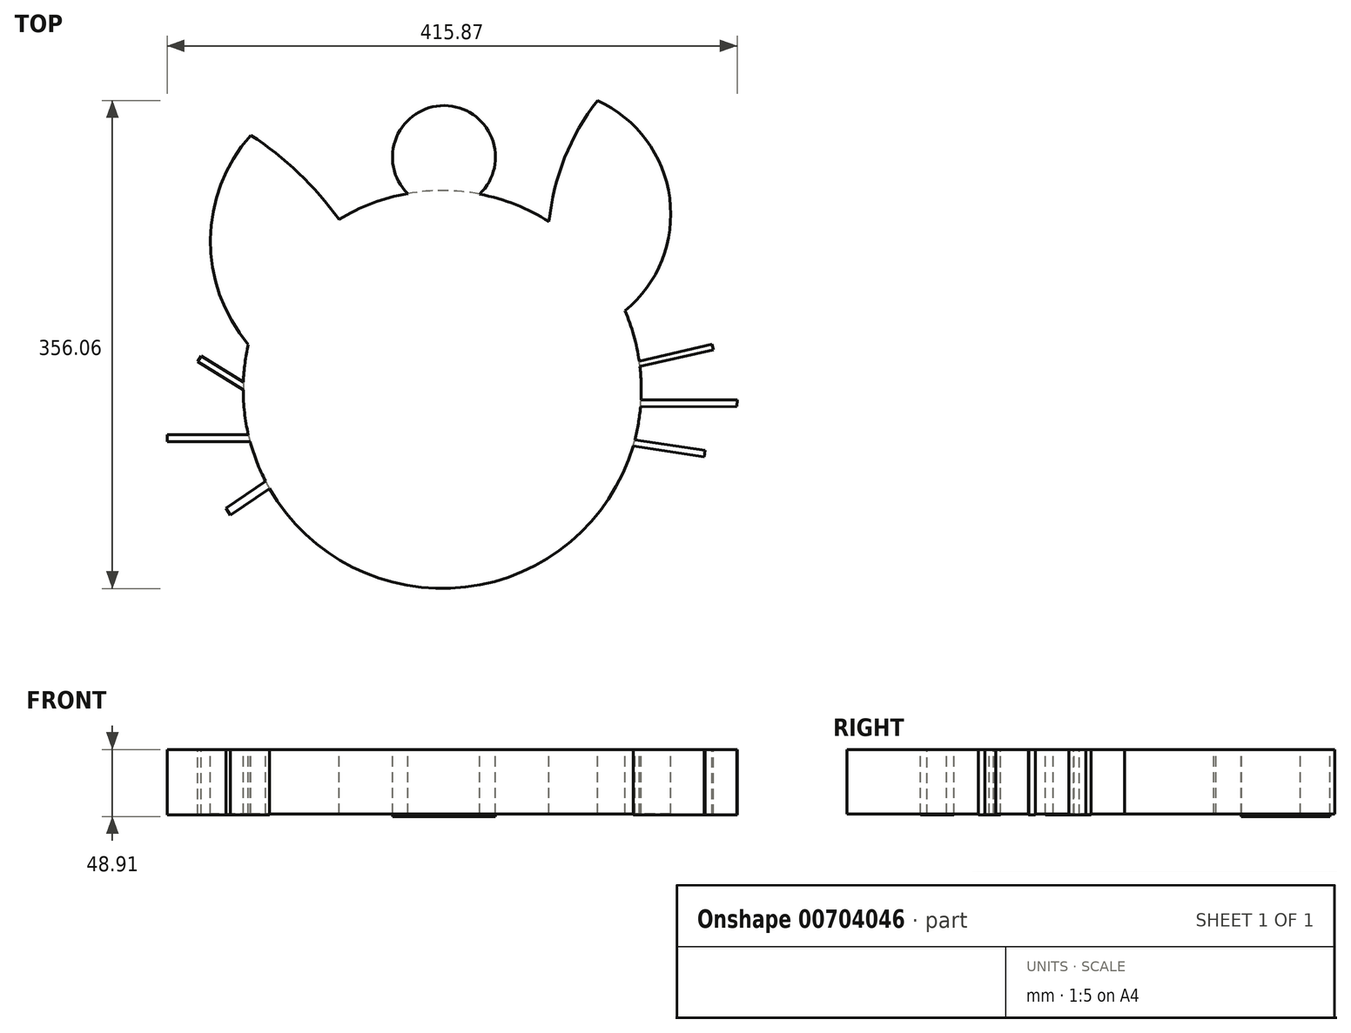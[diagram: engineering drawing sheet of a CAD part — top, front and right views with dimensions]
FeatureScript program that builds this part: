
annotation { "Feature Type Name" : "Feature", "Feature Type Description" : "" }
export const myFeature = defineFeature(function(context is Context, id is Id, definition is map)
    precondition{}
    {
        {
            var Q0;
            Q0=qCreatedBy(makeId("Top.planeOp"),FACE);
            var sketch = newSketch(context, id + "F0", { "sketchPlane" : qUnion([Q0])});
            skCircle(sketch, "E0", {"center": v(70.2, 0) * mm, "radius": 145.22 * mm});
            skArc(sketch, "E1", {"start": v(-5.15, 124.14) * mm, "mid": v(-34.4, 157.96) * mm, "end": v(-69.52, 185.64) * mm});
            skArc(sketch, "E2", {"start": v(-69.52, 185.64) * mm, "mid": v(-98.93, 109.6) * mm, "end": v(-71.24, 32.92) * mm});
            skArc(sketch, "E3", {"start": v(183.54, 210.84) * mm, "mid": v(159.56, 169.2) * mm, "end": v(148.16, 122.52) * mm});
            skArc(sketch, "E4", {"start": v(203.57, 57.46) * mm, "mid": v(236.16, 139.71) * mm, "end": v(183.54, 210.84) * mm});
            skSolve(sketch);
        }
        {
            var Q0;
            Q0 = qSketchRegion(id + "F0", true);
            extrude(context, id + "F1", {"entities" : qUnion([Q0]), "oppositeDirection" : true, "depth" : 46.98 * mm, "offsetDistance" : 25.4 * mm});
        }
        {
            var Q0;
            Q0=makeQuery(id+"F1.opExtrude","CAP_FACE",FACE,{"disambiguationData":[OSD([sQuery(id+"F0.wireOp",EDGE,"E0"),sQuery(id+"F0.wireOp",EDGE,"E1"),sQuery(id+"F0.wireOp",EDGE,"E2"),sQuery(id+"F0.wireOp",EDGE,"E3"),sQuery(id+"F0.wireOp",EDGE,"E4")])],"isStart":true});
            var sketch = newSketch(context, id + "F2", { "sketchPlane" : qUnion([Q0])});
            skArc(sketch, "E5", {"start": v(97.55, 142.62) * mm, "mid": v(71.76, 207.25) * mm, "end": v(45, 143.01) * mm});
            skSolve(sketch);
        }
        {
            var Q0;
            {var subQ0=sQuery(id+"F2.wireOp",EDGE,"E5");Q0=makeQuery(id+"F2.imprint","IMPRINT",FACE,{"disambiguationData":[TD([[makeQuery(id+"F2.imprint","IMPRINT",EDGE,{"derivedFrom":subQ0}),1.0]])]});}
            extrude(context, id + "F3", {"entities" : qUnion([Q0]), "operationType" : NewBodyOperationType.ADD, "oppositeDirection" : true, "depth" : 48.9 * mm, "offsetDistance" : 25.4 * mm});
        }
        {
            var Q0;
            {var subQ0=sQuery(id+"F0.wireOp",EDGE,"E0");Q0=makeQuery(id+"F3.boolean.opBoolean","MERGE",FACE,{"derivedFrom":[makeQuery(id+"F1.opExtrude","CAP_FACE",FACE,{"disambiguationData":[OSD([subQ0,sQuery(id+"F0.wireOp",EDGE,"E1"),sQuery(id+"F0.wireOp",EDGE,"E2"),sQuery(id+"F0.wireOp",EDGE,"E3"),sQuery(id+"F0.wireOp",EDGE,"E4")])],"isStart":true}),makeQuery(id+"F3.opExtrude","CAP_FACE",FACE,{"disambiguationData":[OSD([subQ0,sQuery(id+"F2.wireOp",EDGE,"E5")])],"isStart":true})]});}
            var sketch = newSketch(context, id + "F4", { "sketchPlane" : qUnion([Q0])});
            skSolve(sketch);
        }
        {
            var Q0;
            {var subQ2=sQuery(id+"F0.wireOp",EDGE,"E1");Q0=makeQuery(id+"F4.imprint","IMPRINT",FACE,{"disambiguationData":[TD([[makeQuery(id+"F4.imprint","IMPRINT",EDGE,{"derivedFrom":makeQuery(id+"F1.opExtrude","CAP_EDGE",EDGE,{"disambiguationData":[OSD([subQ2])],"isStart":true})}),1.0]])]});}
            var sketch = newSketch(context, id + "F5", { "sketchPlane" : qUnion([Q0])});
            skLineSegment(sketch, "E6", {"start": v(-66.17, 0) * mm, "end": v(-105.7, 24.6) * mm});
            skLineSegment(sketch, "E7", {"start": v(-65.03, -32.98) * mm, "end": v(-130.48, -32.98) * mm});
            skLineSegment(sketch, "E8", {"start": v(-54.51, -64.23) * mm, "end": v(-87.66, -86.55) * mm});
            skLineSegment(sketch, "E9", {"start": v(-87.66, -86.55) * mm, "end": v(-84.28, -91.56) * mm});
            skLineSegment(sketch, "E10", {"start": v(-84.28, -91.56) * mm, "end": v(-50.29, -68.67) * mm});
            skLineSegment(sketch, "E11", {"start": v(-130.48, -38.07) * mm, "end": v(-65.03, -38.07) * mm});
            skLineSegment(sketch, "E12", {"start": v(-130.48, -32.98) * mm, "end": v(-130.48, -38.07) * mm});
            skLineSegment(sketch, "E13", {"start": v(-105.7, 24.6) * mm, "end": v(-108.36, 20.34) * mm});
            skLineSegment(sketch, "E14", {"start": v(-108.36, 20.34) * mm, "end": v(-68.5, -4.47) * mm});
            skLineSegment(sketch, "E15", {"start": v(212.9, 20.54) * mm, "end": v(267.18, 32.94) * mm});
            skLineSegment(sketch, "E16", {"start": v(267.18, 32.94) * mm, "end": v(268.06, 29.08) * mm});
            skLineSegment(sketch, "E17", {"start": v(268.06, 29.08) * mm, "end": v(211.59, 16.27) * mm});
            skLineSegment(sketch, "E18", {"start": v(213.84, -7.48) * mm, "end": v(285.4, -7.48) * mm});
            skLineSegment(sketch, "E19", {"start": v(285.4, -7.48) * mm, "end": v(285.3, -12.44) * mm});
            skLineSegment(sketch, "E20", {"start": v(285.3, -12.44) * mm, "end": v(208.53, -12.78) * mm});
            skLineSegment(sketch, "E21", {"start": v(209.97, -36.5) * mm, "end": v(262.08, -44.52) * mm});
            skLineSegment(sketch, "E22", {"start": v(262.08, -44.52) * mm, "end": v(261.37, -49.15) * mm});
            skLineSegment(sketch, "E23", {"start": v(261.37, -49.15) * mm, "end": v(205.23, -40.51) * mm});
            skPoint(sketch, "E23.endSnap0", {"position": v(236.02, -40.51) * mm});
            skSolve(sketch);
        }
        {
            var Q0;
            {var subQ0=sQuery(id+"F5.wireOp",EDGE,"E13");Q0=makeQuery(id+"F5.imprint","IMPRINT",FACE,{"disambiguationData":[TD([[makeQuery(id+"F5.imprint","IMPRINT",EDGE,{"derivedFrom":subQ0}),1.0]])]});}
            var Q1;
            {var subQ0=sQuery(id+"F5.wireOp",EDGE,"E12");Q1=makeQuery(id+"F5.imprint","IMPRINT",FACE,{"disambiguationData":[TD([[makeQuery(id+"F5.imprint","IMPRINT",EDGE,{"derivedFrom":subQ0}),1.0]])]});}
            var Q2;
            {var subQ0=sQuery(id+"F5.wireOp",EDGE,"E9");Q2=makeQuery(id+"F5.imprint","IMPRINT",FACE,{"disambiguationData":[TD([[makeQuery(id+"F5.imprint","IMPRINT",EDGE,{"derivedFrom":subQ0}),1.0]])]});}
            var Q3;
            {var subQ0=sQuery(id+"F5.wireOp",EDGE,"E19");Q3=makeQuery(id+"F5.imprint","IMPRINT",FACE,{"disambiguationData":[TD([[makeQuery(id+"F5.imprint","IMPRINT",EDGE,{"derivedFrom":subQ0}),-1.0]])]});}
            var Q4;
            {var subQ0=sQuery(id+"F5.wireOp",EDGE,"E22");Q4=makeQuery(id+"F5.imprint","IMPRINT",FACE,{"disambiguationData":[TD([[makeQuery(id+"F5.imprint","IMPRINT",EDGE,{"derivedFrom":subQ0}),-1.0]])]});}
            var Q5;
            {var subQ0=sQuery(id+"F5.wireOp",EDGE,"E16");Q5=makeQuery(id+"F5.imprint","IMPRINT",FACE,{"disambiguationData":[TD([[makeQuery(id+"F5.imprint","IMPRINT",EDGE,{"derivedFrom":subQ0}),-1.0]])]});}
            extrude(context, id + "F6", {"entities" : qUnion([Q0, Q1, Q2, Q3, Q4, Q5]), "operationType" : NewBodyOperationType.ADD, "oppositeDirection" : true, "depth" : 47.68 * mm, "offsetDistance" : 25.4 * mm});
        }
    });
